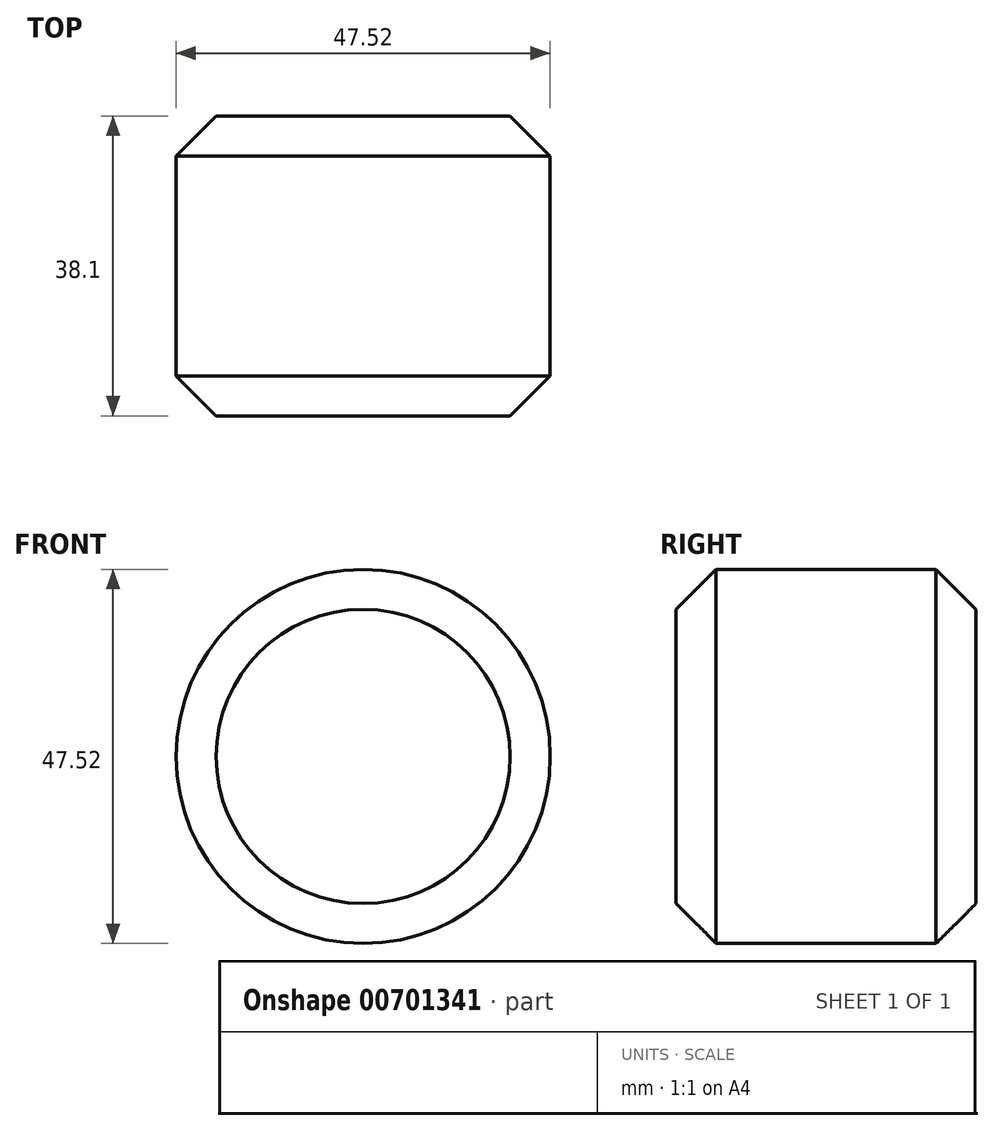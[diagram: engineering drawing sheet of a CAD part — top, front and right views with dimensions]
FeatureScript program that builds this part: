
annotation { "Feature Type Name" : "Feature", "Feature Type Description" : "" }
export const myFeature = defineFeature(function(context is Context, id is Id, definition is map)
    precondition{}
    {
        {
            var Q0;
            Q0=qCreatedBy(makeId("Front.planeOp"),FACE);
            var sketch = newSketch(context, id + "F0", { "sketchPlane" : qUnion([Q0])});
            skCircle(sketch, "E0", {"center": v(0, 0) * mm, "radius": 23.76 * mm});
            skSolve(sketch);
        }
        {
            var Q0;
            Q0=makeQuery(id+"F0.imprint","IMPRINT",FACE,{"disambiguationData":[TD([[makeQuery(id+"F0.imprint","IMPRINT",EDGE,{"derivedFrom":sQuery(id+"F0.wireOp",EDGE,"E0")}),1.0]])]});
            extrude(context, id + "F1", {"entities" : qUnion([Q0]), "depth" : 38.1 * mm, "offsetDistance" : 25.4 * mm});
        }
        {
            var Q0;
            Q0=makeQuery(id+"F1.opExtrude","CAP_FACE",FACE,{"disambiguationData":[OSD([sQuery(id+"F0.wireOp",EDGE,"E0")])],"isStart":false});
            chamfer(context, id + "F2", {"entities" : qUnion([Q0]), "width" : 5.08 * mm, "tangentPropagation" : true});
        }
        {
            var Q0;
            Q0=makeQuery(id+"F1.opExtrude","CAP_FACE",FACE,{"disambiguationData":[OSD([sQuery(id+"F0.wireOp",EDGE,"E0")])],"isStart":true});
            chamfer(context, id + "F3", {"entities" : qUnion([Q0]), "width" : 5.08 * mm, "tangentPropagation" : true});
        }
    });
